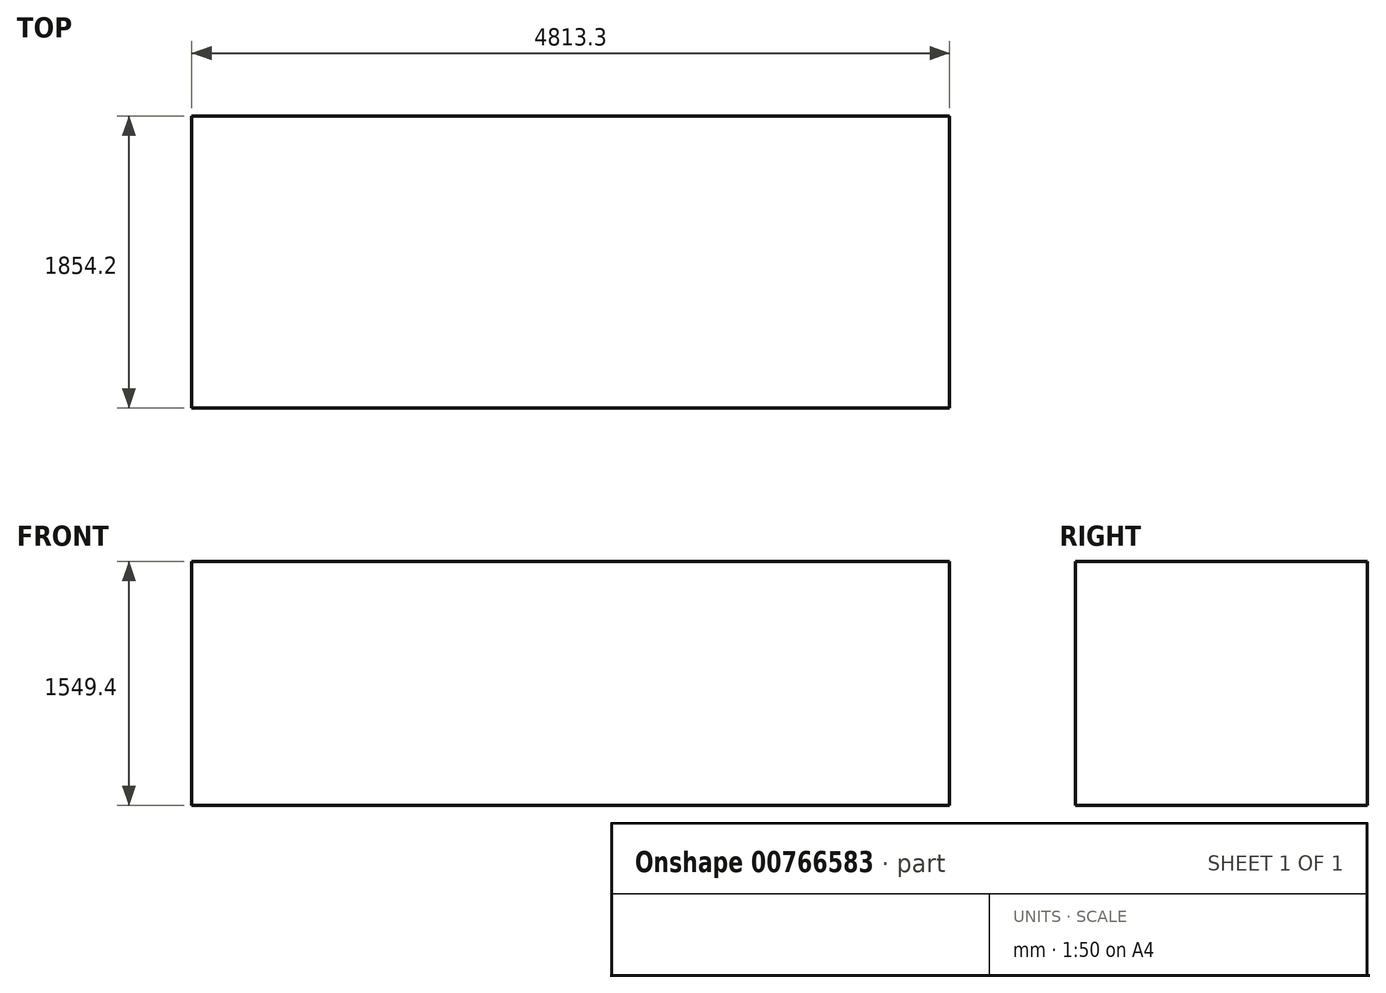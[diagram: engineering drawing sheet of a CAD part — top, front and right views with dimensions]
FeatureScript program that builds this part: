
annotation { "Feature Type Name" : "Feature", "Feature Type Description" : "" }
export const myFeature = defineFeature(function(context is Context, id is Id, definition is map)
    precondition{}
    {
        {
            var Q0;
            Q0=qCreatedBy(makeId("Top.planeOp"),FACE);
            var sketch = newSketch(context, id + "F0", { "sketchPlane" : qUnion([Q0])});
            skLineSegment(sketch, "E0.bottom", {"start": v(-2406.65, 927.1) * mm, "end": v(2406.65, 927.1) * mm});
            skLineSegment(sketch, "E0.top", {"start": v(-2406.65, -927.1) * mm, "end": v(2406.65, -927.1) * mm});
            skLineSegment(sketch, "E0.left", {"start": v(-2406.65, 927.1) * mm, "end": v(-2406.65, -927.1) * mm});
            skLineSegment(sketch, "E0.right", {"start": v(2406.65, 927.1) * mm, "end": v(2406.65, -927.1) * mm});
            skLineSegment(sketch, "E1", {"start": v(-2406.65, 927.1) * mm, "end": v(2406.65, -927.1) * mm});
            skSolve(sketch);
        }
        {
            var Q0;
            Q0 = qSketchRegion(id + "F0", true);
            extrude(context, id + "F1", {"entities" : qUnion([Q0]), "depth" : 1549.4 * mm, "offsetDistance" : 25.4 * mm});
        }
    });
